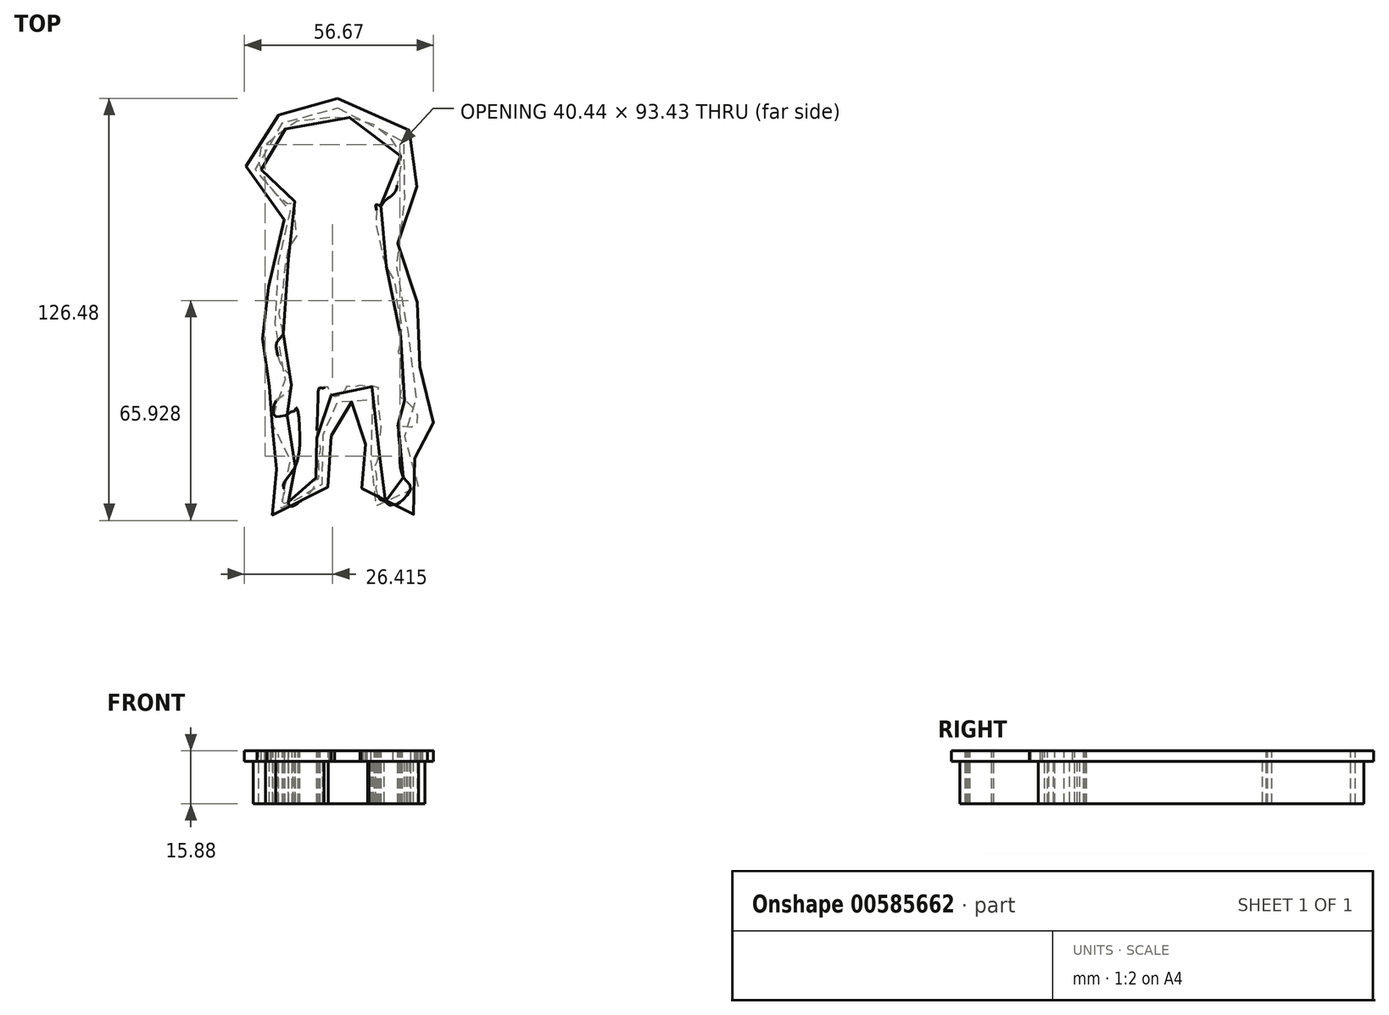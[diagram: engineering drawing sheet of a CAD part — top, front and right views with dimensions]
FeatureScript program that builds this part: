
annotation { "Feature Type Name" : "Feature", "Feature Type Description" : "" }
export const myFeature = defineFeature(function(context is Context, id is Id, definition is map)
    precondition{}
    {
        {
            var Q0;
            Q0=qCreatedBy(makeId("Top.planeOp"),FACE);
            var sketch = newSketch(context, id + "F0", { "sketchPlane" : qUnion([Q0])});
            skLineSegment(sketch, "E0.bottom", {"start": v(38.1, -63.5) * mm, "end": v(-38.1, -63.5) * mm});
            skLineSegment(sketch, "E0.top", {"start": v(38.1, 63.5) * mm, "end": v(-38.1, 63.5) * mm});
            skLineSegment(sketch, "E0.left", {"start": v(38.1, -63.5) * mm, "end": v(38.1, 63.5) * mm});
            skLineSegment(sketch, "E0.right", {"start": v(-38.1, -63.5) * mm, "end": v(-38.1, 63.5) * mm});
            skPoint(sketch, "E0.middle", {"position": v(0, 0) * mm});
            skFitSpline(sketch, "E1", {"points": [v(-16.27, -7.82) * mm, v(-16.92, -3.77) * mm, v(-17.57, 0) * mm, v(-16.27, 5.14) * mm, v(-16.1, 10.33) * mm, v(-14.81, 14.22) * mm, v(-14.65, 18.11) * mm, v(-13.36, 20.53) * mm, v(-11.92, 21.81) * mm, v(-12.35, 24.99) * mm, v(-12.78, 27.4) * mm, v(-12.6, 28.5) * mm, v(-13.04, 32.28) * mm, v(-13.55, 31.94) * mm, v(-14.5, 31.08) * mm, v(-15.35, 31.25) * mm, v(-16.38, 32.2) * mm, v(-18.18, 33.83) * mm, v(-20.24, 35.28) * mm, v(-21.78, 38.97) * mm, v(-23.36, 42.86) * mm, v(-23.57, 45.67) * mm, v(-22.95, 47.85) * mm, v(-21.28, 49) * mm, v(-19.93, 49.93) * mm, v(-19, 51.5) * mm, v(-17.44, 52.53) * mm, v(-15.46, 53.78) * mm, v(-13.18, 55.76) * mm, v(-10.7, 55.89) * mm, v(-8.48, 56.14) * mm, v(-5.39, 57.13) * mm, v(-1.3, 57.25) * mm, v(4.5, 56.88) * mm, v(8.22, 55.76) * mm, v(11.3, 54.78) * mm, v(14.15, 52.67) * mm, v(17.74, 48.34) * mm, v(18.85, 46.24) * mm, v(18.97, 45.38) * mm, v(19.47, 44.51) * mm, v(18.23, 40.3) * mm, v(17.86, 37.1) * mm, v(17.5, 35.11) * mm, v(15.64, 33.13) * mm, v(13.9, 31.77) * mm, v(13.04, 30.66) * mm, v(11.55, 30.9) * mm, v(11.68, 29.3) * mm, v(11.55, 24.1) * mm, v(12.42, 21.26) * mm, v(12.91, 18.66) * mm, v(14.28, 13.34) * mm, v(16.75, 8.52) * mm, v(17.5, 6.67) * mm, v(17.61, 2.96) * mm, v(18.1, 0) * mm, v(18.97, -3.47) * mm, v(18.73, -10.52) * mm, v(18.23, -13.12) * mm, v(18.85, -15.72) * mm, v(19.22, -19.3) * mm, v(19.22, -23.5) * mm, v(18.85, -26.97) * mm, v(21.2, -28.46) * mm, v(22.2, -29.7) * mm, v(23.18, -30.44) * mm, v(24.05, -33.28) * mm, v(23.67, -34.76) * mm, v(22.8, -35.75) * mm, v(21.08, -35.63) * mm, v(19.1, -35.38) * mm, v(18.1, -34.89) * mm, v(18.36, -36.74) * mm, v(18.36, -38.47) * mm, v(18.6, -40.95) * mm, v(18.73, -43.8) * mm, v(18.6, -45.52) * mm, v(18.97, -48.24) * mm, v(19.6, -50.6) * mm, v(21.2, -52.45) * mm, v(21.94, -53.93) * mm, v(20.46, -56.65) * mm, v(18.85, -58.14) * mm, v(17.86, -58.88) * mm, v(16.75, -58.88) * mm, v(16.25, -59.25) * mm, v(15.14, -58.76) * mm, v(14.03, -57.9) * mm, v(12.8, -57.52) * mm, v(11.8, -55.42) * mm, v(11.55, -53.44) * mm, v(11.93, -51.46) * mm, v(11.43, -48.86) * mm, v(11.18, -47.25) * mm, v(12.42, -45.03) * mm, v(12.3, -40.58) * mm, v(12.8, -38.47) * mm, v(13.04, -35.14) * mm, v(12.17, -27.1) * mm, v(11.93, -23.39) * mm, v(9.33, -23.88) * mm, v(7.97, -23.26) * mm, v(6.11, -23.5) * mm, v(4.63, -23.76) * mm, v(2.53, -23.63) * mm, v(2.03, -25) * mm, v(1.17, -25.86) * mm, v(0, -26.73) * mm, v(-1.8, -26.23) * mm, v(-2.8, -24.62) * mm, v(-2.8, -23.5) * mm, v(-3.53, -23.63) * mm, v(-4.4, -24.13) * mm, v(-5.39, -24) * mm, v(-5.88, -28.83) * mm, v(-6.25, -38.72) * mm, v(-6, -39.83) * mm, v(-5.27, -41.57) * mm, v(-5.27, -43.17) * mm, v(-5.88, -44.78) * mm, v(-5.88, -45.65) * mm, v(-5.64, -48.24) * mm, v(-5.64, -49.98) * mm, v(-6, -51.58) * mm, v(-6.5, -50.97) * mm, v(-7, -53.31) * mm, v(-7.86, -54.92) * mm, v(-9.22, -56.53) * mm, v(-10.58, -57.9) * mm, v(-11.33, -58.01) * mm, v(-12.44, -59) * mm, v(-14.17, -59.37) * mm, v(-14.66, -58.5) * mm, v(-14.66, -58.14) * mm, v(-15.65, -58.63) * mm, v(-16.4, -58.26) * mm, v(-16.52, -57.15) * mm, v(-16.15, -55.91) * mm, v(-15.78, -55.05) * mm, v(-16.27, -53.93) * mm, v(-16.02, -52.45) * mm, v(-14.91, -50.84) * mm, v(-12.56, -47.25) * mm, v(-11.33, -41.07) * mm, v(-11.57, -32.9) * mm, v(-12.2, -29.94) * mm, v(-12.8, -30.93) * mm, v(-14.42, -31.42) * mm, v(-14.79, -31.92) * mm, v(-16.9, -32.54) * mm, v(-18.62, -32.54) * mm, v(-19.24, -31.55) * mm, v(-19, -29.32) * mm, v(-18, -27.34) * mm, v(-16.02, -26.1) * mm, v(-14.17, -24.38) * mm, v(-13.8, -23.14) * mm, v(-13.55, -21.4) * mm, v(-14.67, -19.8) * mm, v(-15.53, -18.93) * mm, v(-17, -16.72) * mm, v(-18, -13.76) * mm, v(-18.11, -10.31) * mm, v(-16.27, -7.82) * mm]});
            skFitSpline(sketch, "E2", {"points": [v(0, 59.86) * mm, v(5.89, 59) * mm, v(13.44, 56.67) * mm, v(19.69, 49.99) * mm, v(22.6, 43.45) * mm, v(21.86, 41.7) * mm, v(20.7, 38.08) * mm, v(20.27, 33.14) * mm, v(14.45, 28.5) * mm, v(14.15, 25.52) * mm, v(16.97, 13.5) * mm, v(20.09, 7.86) * mm, v(20.53, 2.67) * mm, v(21.57, -3.57) * mm, v(20.83, -12.47) * mm, v(21.87, -19.3) * mm, v(21.57, -25.24) * mm, v(23.06, -26.57) * mm, v(25.73, -30.88) * mm, v(25.73, -36.37) * mm, v(23.95, -37.7) * mm, v(20.24, -37.7) * mm, v(20.53, -40.52) * mm, v(20.68, -44.38) * mm, v(21.13, -48.98) * mm, v(23.06, -51.06) * mm, v(24.24, -54.03) * mm, v(22.46, -57.89) * mm, v(18.9, -60.41) * mm, v(15.63, -61.16) * mm, v(11.63, -59.37) * mm, v(9.4, -55.81) * mm, v(9.85, -52.7) * mm, v(9.85, -50.32) * mm, v(9.1, -47.65) * mm, v(10.59, -44.38) * mm, v(10.59, -40.67) * mm, v(11.33, -36.81) * mm, v(10.74, -31.47) * mm, v(10.3, -26.28) * mm, v(9.25, -26.13) * mm, v(7.03, -25.68) * mm, v(3.76, -25.53) * mm, v(1.98, -27.32) * mm, v(0, -28.35) * mm, v(-2.92, -27.9) * mm, v(-3.96, -26.87) * mm, v(-4.25, -27.46) * mm, v(-4.25, -32.8) * mm, v(-4.4, -38.15) * mm, v(-3.07, -41.56) * mm, v(-3.07, -44.24) * mm, v(-4.25, -46.16) * mm, v(-4.1, -50.47) * mm, v(-5.74, -54.77) * mm, v(-8.86, -58.63) * mm, v(-10.58, -60.26) * mm, v(-14.5, -61) * mm, v(-16.72, -60.26) * mm, v(-18.5, -57.9) * mm, v(-17.9, -54.77) * mm, v(-17.76, -51.5) * mm, v(-14.91, -47.2) * mm, v(-13.46, -42.3) * mm, v(-13.16, -33.55) * mm, v(-14.91, -33.55) * mm, v(-18.35, -34.59) * mm, v(-21.32, -32.66) * mm, v(-21.03, -28.95) * mm, v(-18.8, -24.94) * mm, v(-14.91, -22.71) * mm, v(-17.02, -20.2) * mm, v(-20.28, -14.25) * mm, v(-20.13, -9.65) * mm, v(-18.5, -6.98) * mm, v(-19.4, -1.79) * mm, v(-19.1, 2.81) * mm, v(-18.06, 8.6) * mm, v(-17.76, 12.76) * mm, v(-16.57, 18.25) * mm, v(-14.91, 23) * mm, v(-13.57, 23.62) * mm, v(-13.98, 26.53) * mm, v(-14.23, 29.36) * mm, v(-14.91, 29.36) * mm, v(-17.48, 30.86) * mm, v(-21.38, 33.68) * mm, v(-24.21, 40.17) * mm, v(-25.12, 46.73) * mm, v(-22.71, 50.8) * mm, v(-20.14, 52.8) * mm, v(-16.73, 55.13) * mm, v(-13.57, 58.2) * mm, v(-8.91, 58.87) * mm, v(-4.59, 59.62) * mm, v(0, 59.86) * mm]});
            skSolve(sketch);
        }
        {
            var Q0;
            Q0=sQuery(id+"F0.wireOp",EDGE,"E1");
            extrude(context, id + "F1", {"bodyType" : ToolBodyType.SURFACE, "surfaceEntities" : qUnion([Q0]), "depth" : 12.7 * mm, "offsetDistance" : 25.4 * mm});
        }
        {
            var Q0;
            Q0=makeQuery(id+"F0.imprint","IMPRINT",FACE,{"disambiguationData":[TD([[makeQuery(id+"F0.imprint","IMPRINT",EDGE,{"derivedFrom":sQuery(id+"F0.wireOp",EDGE,"E1")}),-1.0]])]});
            var Q1;
            Q1=sQuery(id+"F0.wireOp",EDGE,"E1");
            extrude(context, id + "F2", {"entities" : qUnion([Q0]), "bodyType" : ToolBodyType.SURFACE, "surfaceEntities" : qUnion([Q1]), "oppositeDirection" : true, "depth" : 6.35 * mm, "offsetDistance" : 25.4 * mm});
        }
        {
            var Q0;
            Q0=makeQuery(id+"F2.opExtrude","SWEPT_BODY",BODY,{"disambiguationData":[OSD([sQuery(id+"F0.wireOp",EDGE,"E1")])]});
            deleteBodies(context, id + "F3", {"entities" : qUnion([Q0])});
        }
        {
            var Q0;
            Q0=makeQuery(id+"F0.imprint","IMPRINT",FACE,{"disambiguationData":[TD([[makeQuery(id+"F0.imprint","IMPRINT",EDGE,{"derivedFrom":sQuery(id+"F0.wireOp",EDGE,"E1")}),1.0]])]});
            extrude(context, id + "F4", {"entities" : qUnion([Q0]), "depth" : 12.7 * mm, "offsetDistance" : 25.4 * mm});
        }
        {
            var Q0;
            Q0=makeQuery(id+"F4.opExtrude","CAP_FACE",FACE,{"disambiguationData":[OSD([sQuery(id+"F0.wireOp",EDGE,"E1"),sQuery(id+"F0.wireOp",EDGE,"E2")])],"isStart":false});
            var sketch = newSketch(context, id + "F5", { "sketchPlane" : qUnion([Q0])});
            skFitSpline(sketch, "E3", {"points": [v(0, 62.7) * mm, v(9.62, 61.4) * mm, v(19.54, 55.52) * mm, v(24.7, 46.33) * mm, v(25.14, 41.01) * mm, v(23.56, 38.14) * mm, v(23.84, 33.54) * mm, v(16.95, 26.65) * mm, v(17.67, 20.76) * mm, v(19.68, 14.58) * mm, v(23.13, 8.26) * mm, v(23.7, 2.51) * mm, v(24.85, -3.66) * mm, v(23.41, -10.99) * mm, v(24.7, -18.31) * mm, v(23.84, -23.92) * mm, v(27, -26.79) * mm, v(28.73, -34.98) * mm, v(26.29, -40.3) * mm, v(21.98, -40) * mm, v(22.98, -43.17) * mm, v(23.27, -47.47) * mm, v(26.43, -51.35) * mm, v(25, -59.68) * mm, v(17.24, -63.7) * mm, v(7.76, -60.55) * mm, v(7.47, -53.22) * mm, v(7.47, -49.92) * mm, v(6.9, -46.61) * mm, v(8.76, -43.6) * mm, v(8.33, -40.3) * mm, v(9.62, -36.84) * mm, v(8.48, -28.37) * mm, v(4.6, -27.94) * mm, v(1.87, -30.38) * mm, v(-2.44, -30.96) * mm, v(-2.3, -33.54) * mm, v(-1.72, -39.14) * mm, v(-0.92, -42.1) * mm, v(-1.84, -46.54) * mm, v(-2.03, -50.61) * mm, v(-5.82, -59.13) * mm, v(-12.67, -63.38) * mm, v(-19.52, -62.09) * mm, v(-21, -56.53) * mm, v(-19.99, -54.4) * mm, v(-20.08, -51.17) * mm, v(-17.58, -47.56) * mm, v(-14.99, -40.8) * mm, v(-15.36, -37.1) * mm, v(-17.58, -36.63) * mm, v(-22.11, -36.91) * mm, v(-23.97, -32.28) * mm, v(-22.76, -25.34) * mm, v(-18.87, -22.47) * mm, v(-18.69, -21.55) * mm, v(-21.74, -17.47) * mm, v(-22.76, -10.53) * mm, v(-21.19, -6.55) * mm, v(-20.82, -4.7) * mm, v(-21.93, 1.32) * mm, v(-20.26, 7.89) * mm, v(-19.25, 18.53) * mm, v(-16.38, 24.64) * mm, v(-16.47, 27.88) * mm, v(-22.74, 31.38) * mm, v(-26.82, 39.98) * mm, v(-27.37, 49.02) * mm, v(-21.3, 55.2) * mm, v(-17.89, 57.5) * mm, v(-14.5, 60.89) * mm, v(-9.26, 61.58) * mm, v(0, 62.7) * mm]});
            skSolve(sketch);
        }
        {
            var Q0;
            Q0=makeQuery(id+"F5.imprint","IMPRINT",FACE,{"disambiguationData":[TD([[makeQuery(id+"F5.imprint","IMPRINT",EDGE,{"derivedFrom":sQuery(id+"F5.wireOp",EDGE,"E3")}),-1.0]])]});
            var Q1;
            Q1=makeQuery(id+"F5.imprint","IMPRINT",FACE,{"disambiguationData":[TD([[makeQuery(id+"F5.imprint","IMPRINT",EDGE,{"derivedFrom":makeQuery(id+"F4.opExtrude","CAP_EDGE",EDGE,{"disambiguationData":[OSD([sQuery(id+"F0.wireOp",EDGE,"E1")])],"isStart":false})}),1.0]])]});
            extrude(context, id + "F6", {"entities" : qUnion([Q0, Q1]), "operationType" : NewBodyOperationType.ADD, "depth" : 3.17 * mm, "offsetDistance" : 25.4 * mm});
        }
    });
